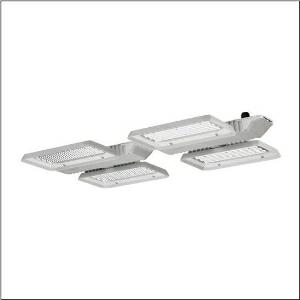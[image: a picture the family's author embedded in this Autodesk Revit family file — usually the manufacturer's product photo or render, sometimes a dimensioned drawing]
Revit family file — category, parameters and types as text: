
# Revit family: highbay_11_51hla2d24mcad
name_source: partatom
category: Lighting Fixtures
units: mm (PartAtom-declared; Revit-internal decimal feet)

## family parameters
Cut with Voids When Loaded = No
Host = Face
Light Source = No
Part Type = Normal
Room Calculation Point = No
Round Connector Dimension = Use Diameter
Shared = No

## types (1)
- --- (1 x LED, 4320 lm, 28.2 W, 4000K)
    Apparent Load = 28 VA
    CIE Flux Codes = 89 96 99 100 100
    Color Rendering = 80
    Color Temperature = 4000K
    Default Elevation = 1800 mm
    Description = Highbay 11, LED high bay luminaire, primary light control with lens, of PMMA, light emission: direct distribution, primary light characteristic: symmetric, installation type: suspended mounting, surface-mounted, for 2x 2 x LED rated luminous flux: 28.800 lm, light colour: 840, colour temperature: 4000K, control gear: ECG DALI, with terminal, 5-pole, max. 2.5mm², mains connection: 230..240V, AC/DC, 50/60Hz, rated input power: 162W, LED unit, of diecast aluminium, bead blasted, unplated, silver, length: 940 mm, width: 500 mm, height: 65mm, housing, of diecast aluminium, bead blasted, uncoated, silver, protection rating (complete): IP65, insulation class (complete): insulation class I (protective earthing), certification: CE, protection symbol: D, impact resistance: IK08 with glass or PC cover, permissible ambient temperature for indoor applications: -35..+55°C, standard: EN 60598-2-22, reducing of maximum allowable ambient temperature of 5°C with ceiling mounting, corresponds to IFS (International Featured Standards) requirements for safety and quality in the food industry, packaging unit: 1 piece
    Height = 95 mm
    Lamp = 1 x LED
    Lamp Light Flux = 4320 lm
    Lamp Power = 28.2 W
    Lamp count = 1
    Length = 939 mm
    Luminous efficacy = 153 lm/W
    Manufacturer = Siteco
    ModVariant = No
    Model = 51HLA2D24MCAD
    Mounting Place = Ceiling
    Mounting Type = Pendant
    Number of Poles = 1
    OnlyDefault = Yes
    Power Factor = 1
    Product Name = Highbay 11
    Product group = LED high bay luminaire
    ProductGroupID = 903
    Protection Class = Protection class I
    Protection Degree = IP 65
    RLX_Detail_Level = 1
    RlxData = <blob elided: 104609 chars, md5=668a4420>
    Socket = socket
    Standby Power = 0 W
    System Light Flux = 4320 lm
    System Power = 28 W
    Type Comments = : central accumulator DC – ECG emengency level 15%
    Type Image = l_1003428.jpg
    URL = http://relux.com
    VarID = @adj_128323
    Voltage = 0 V
    Weight = 0.00 kg
    Width = 501 mm

## geometry (parser evidence)
native form markers: Blend x4, Sweep x12
no freeform markers — native parametric forms only
